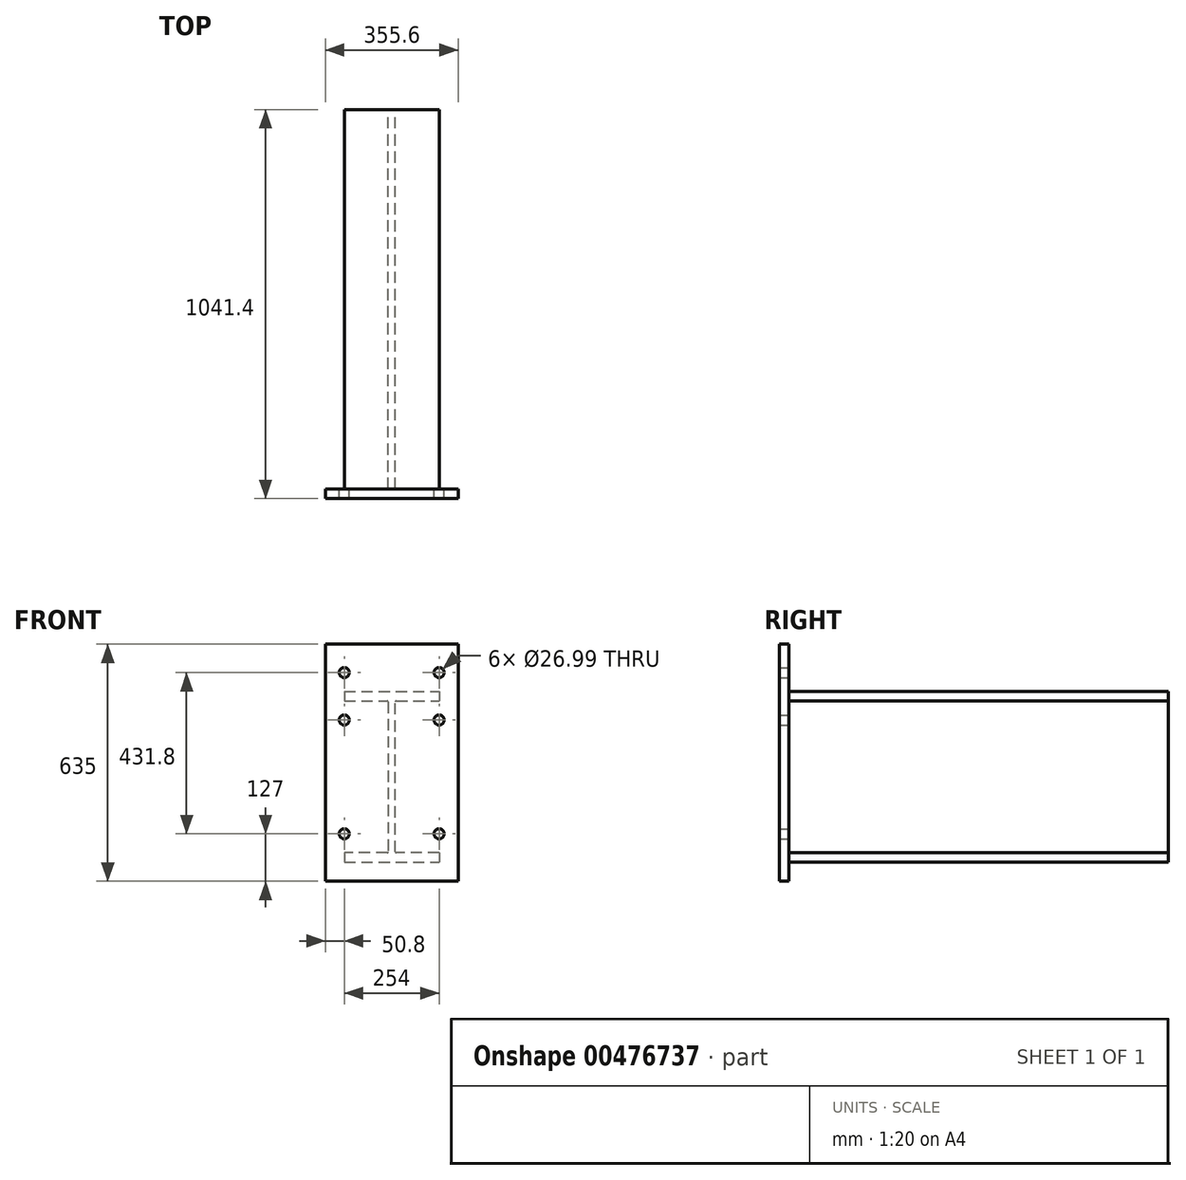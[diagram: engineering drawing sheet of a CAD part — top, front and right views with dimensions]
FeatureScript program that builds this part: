
annotation { "Feature Type Name" : "Feature", "Feature Type Description" : "" }
export const myFeature = defineFeature(function(context is Context, id is Id, definition is map)
    precondition{}
    {
        {
            var Q0;
            Q0=qCreatedBy(makeId("Front.planeOp"),FACE);
            var sketch = newSketch(context, id + "F0", { "sketchPlane" : qUnion([Q0])});
            skLineSegment(sketch, "E0", {"start": v(127, -203.2) * mm, "end": v(12.06, -203.2) * mm});
            skLineSegment(sketch, "E1", {"start": v(9.52, -200.66) * mm, "end": v(9.52, 200.66) * mm});
            skLineSegment(sketch, "E2", {"start": v(12.06, 203.2) * mm, "end": v(127, 203.2) * mm});
            skLineSegment(sketch, "E3", {"start": v(-127, 203.2) * mm, "end": v(-12.06, 203.2) * mm});
            skLineSegment(sketch, "E4", {"start": v(-9.53, 200.66) * mm, "end": v(-9.53, -200.66) * mm});
            skLineSegment(sketch, "E5", {"start": v(-12.06, -203.2) * mm, "end": v(-127, -203.2) * mm});
            skLineSegment(sketch, "E6", {"start": v(0, 0) * mm, "end": v(-9.52, 0) * mm, "construction": true});
            skLineSegment(sketch, "E7", {"start": v(0, 0) * mm, "end": v(9.52, 0) * mm, "construction": true});
            skLineSegment(sketch, "E8", {"start": v(0, 0) * mm, "end": v(0, 228.6) * mm, "construction": true});
            skLineSegment(sketch, "E9", {"start": v(0, 0) * mm, "end": v(0, -228.6) * mm, "construction": true});
            skPoint(sketch, "E10.visualSharp", {"position": v(-9.53, 203.2) * mm});
            skArc(sketch, "E10.filletArc", {"start": v(-9.52, 200.66) * mm, "mid": v(-10.27, 202.46) * mm, "end": v(-12.06, 203.2) * mm});
            skPoint(sketch, "E11.visualSharp", {"position": v(9.53, 203.2) * mm});
            skArc(sketch, "E11.filletArc", {"start": v(12.06, 203.2) * mm, "mid": v(10.27, 202.46) * mm, "end": v(9.52, 200.66) * mm});
            skPoint(sketch, "E12.visualSharp", {"position": v(9.53, -203.2) * mm});
            skArc(sketch, "E12.filletArc", {"start": v(9.52, -200.66) * mm, "mid": v(10.27, -202.46) * mm, "end": v(12.06, -203.2) * mm});
            skPoint(sketch, "E13.visualSharp", {"position": v(-9.53, -203.2) * mm});
            skArc(sketch, "E13.filletArc", {"start": v(-12.06, -203.2) * mm, "mid": v(-10.27, -202.46) * mm, "end": v(-9.52, -200.66) * mm});
            skPoint(sketch, "E14.visualSharp", {"position": v(-127, 228.6) * mm});
            skPoint(sketch, "E15.visualSharp", {"position": v(127, 228.6) * mm});
            skPoint(sketch, "E16.visualSharp", {"position": v(127, 203.2) * mm});
            skPoint(sketch, "E17.visualSharp", {"position": v(127, -228.6) * mm});
            skPoint(sketch, "E18.visualSharp", {"position": v(-127, -203.2) * mm});
            skPoint(sketch, "E19.visualSharp", {"position": v(-127, -228.6) * mm});
            skLineSegment(sketch, "E20", {"start": v(127, -203.2) * mm, "end": v(127, -228.6) * mm});
            skLineSegment(sketch, "E21", {"start": v(-127, -203.2) * mm, "end": v(-127, -228.6) * mm});
            skLineSegment(sketch, "E22", {"start": v(-127, 228.6) * mm, "end": v(-127, 203.2) * mm});
            skLineSegment(sketch, "E23", {"start": v(127, 228.6) * mm, "end": v(127, 203.2) * mm});
            skLineSegment(sketch, "E24", {"start": v(-127, 228.6) * mm, "end": v(127, 228.6) * mm});
            skLineSegment(sketch, "E25", {"start": v(-127, -228.6) * mm, "end": v(127, -228.6) * mm});
            skSolve(sketch);
        }
        {
            var Q0;
            Q0=makeQuery(id+"F0.imprint","IMPRINT",FACE,{"disambiguationData":[TD([[makeQuery(id+"F0.imprint","IMPRINT",EDGE,{"derivedFrom":sQuery(id+"F0.wireOp",EDGE,"E0")}),1.0]])]});
            extrude(context, id + "F1", {"entities" : qUnion([Q0]), "endBound" : BoundingType.SYMMETRIC, "depth" : 1016 * mm});
        }
        {
            var Q0;
            Q0=makeQuery(id+"F1.opExtrude","CAP_FACE",FACE,{"disambiguationData":[OSD([sQuery(id+"F0.wireOp",EDGE,"E0"),sQuery(id+"F0.wireOp",EDGE,"E1"),sQuery(id+"F0.wireOp",EDGE,"E2"),sQuery(id+"F0.wireOp",EDGE,"E3"),sQuery(id+"F0.wireOp",EDGE,"E4"),sQuery(id+"F0.wireOp",EDGE,"E5"),sQuery(id+"F0.wireOp",EDGE,"E10.filletArc"),sQuery(id+"F0.wireOp",EDGE,"E11.filletArc"),sQuery(id+"F0.wireOp",EDGE,"E12.filletArc"),sQuery(id+"F0.wireOp",EDGE,"E13.filletArc"),sQuery(id+"F0.wireOp",EDGE,"E20"),sQuery(id+"F0.wireOp",EDGE,"E21"),sQuery(id+"F0.wireOp",EDGE,"E22"),sQuery(id+"F0.wireOp",EDGE,"E23"),sQuery(id+"F0.wireOp",EDGE,"E24"),sQuery(id+"F0.wireOp",EDGE,"E25")])],"isStart":false});
            var sketch = newSketch(context, id + "F2", { "sketchPlane" : qUnion([Q0])});
            skLineSegment(sketch, "E26", {"start": v(-177.8, 355.6) * mm, "end": v(177.8, 355.6) * mm});
            skLineSegment(sketch, "E27", {"start": v(177.8, 355.6) * mm, "end": v(177.8, -279.4) * mm});
            skLineSegment(sketch, "E28", {"start": v(177.8, -279.4) * mm, "end": v(-177.8, -279.4) * mm});
            skLineSegment(sketch, "E29", {"start": v(-177.8, -279.4) * mm, "end": v(-177.8, 355.6) * mm});
            skPoint(sketch, "E30", {"position": v(-127, 279.4) * mm});
            skPoint(sketch, "E31", {"position": v(127, 279.4) * mm});
            skPoint(sketch, "E32", {"position": v(127, 152.4) * mm});
            skPoint(sketch, "E33", {"position": v(-127, 152.4) * mm});
            skPoint(sketch, "E34", {"position": v(-127, -152.4) * mm});
            skPoint(sketch, "E35", {"position": v(127, -152.4) * mm});
            skSolve(sketch);
        }
        {
            var Q0;
            Q0=makeQuery(id+"F2.imprint","IMPRINT",FACE,{"disambiguationData":[TD([[makeQuery(id+"F2.imprint","IMPRINT",EDGE,{"derivedFrom":sQuery(id+"F2.wireOp",EDGE,"E26")}),-1.0]])]});
            var Q1;
            Q1=makeQuery(id+"F2.imprint","IMPRINT",FACE,{"disambiguationData":[TD([[makeQuery(id+"F2.imprint","IMPRINT",EDGE,{"derivedFrom":makeQuery(id+"F1.opExtrude","CAP_EDGE",EDGE,{"disambiguationData":[OSD([sQuery(id+"F0.wireOp",EDGE,"E0")])],"isStart":false})}),1.0]])]});
            extrude(context, id + "F3", {"entities" : qUnion([Q0, Q1]), "depth" : 25.4 * mm});
        }
        {
            var Q0;
            Q0=sQuery(id+"F2.wireOp",VERTEX,"E31");
            var Q1;
            Q1=sQuery(id+"F2.wireOp",VERTEX,"E32");
            var Q2;
            Q2=sQuery(id+"F2.wireOp",VERTEX,"E35");
            var Q3;
            Q3=sQuery(id+"F2.wireOp",VERTEX,"E34");
            var Q4;
            Q4=sQuery(id+"F2.wireOp",VERTEX,"E33");
            var Q5;
            Q5=sQuery(id+"F2.wireOp",VERTEX,"E30");
            var Q6;
            Q6=makeQuery(id+"F3.opExtrude","SWEPT_BODY",BODY,{"disambiguationData":[OSD([sQuery(id+"F2.wireOp",EDGE,"E26"),sQuery(id+"F2.wireOp",EDGE,"E27"),sQuery(id+"F2.wireOp",EDGE,"E28"),sQuery(id+"F2.wireOp",EDGE,"E29")])]});
            hole(context, id + "F4", {"style" : HoleStyle.SIMPLE, "endStyle" : HoleEndStyle.BLIND, "oppositeDirection" : true, "holeDiameter" : 26.99 * mm, "holeDepth" : 25.4 * mm, "isTappedThrough" : true, "tappedDepth" : 12.7 * mm, "tapClearance" : 3, "locations" : qUnion([Q0, Q1, Q2, Q3, Q4, Q5]), "scope" : qUnion([Q6])});
        }
    });
